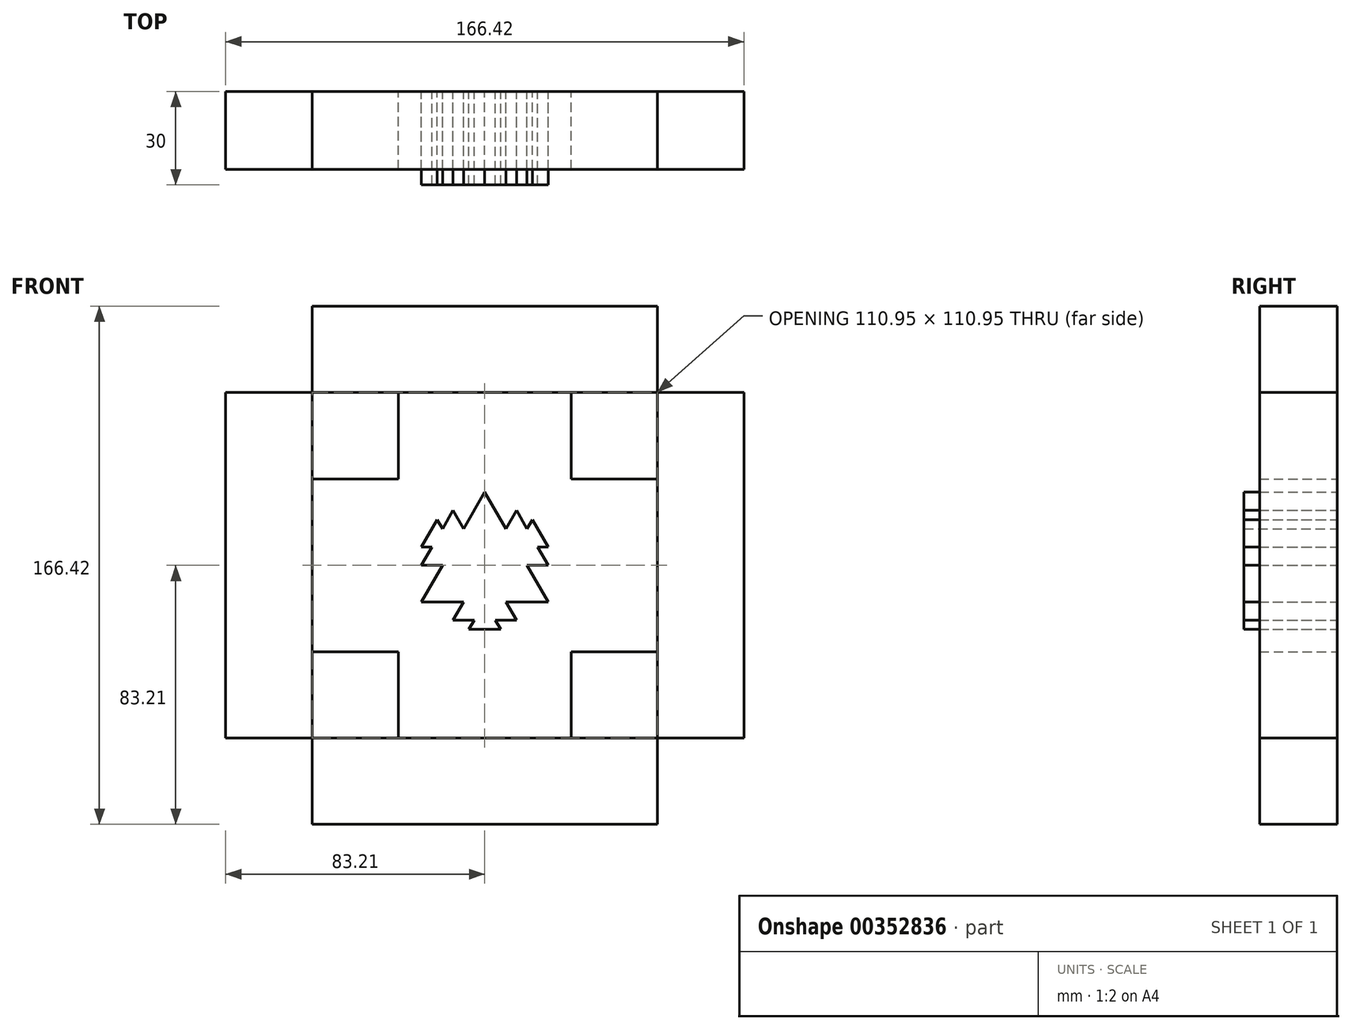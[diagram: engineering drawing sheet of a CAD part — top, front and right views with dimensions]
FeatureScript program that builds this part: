
annotation { "Feature Type Name" : "Feature", "Feature Type Description" : "" }
export const myFeature = defineFeature(function(context is Context, id is Id, definition is map)
    precondition{}
    {
        {
            var Q0;
            Q0=qCreatedBy(makeId("Front.planeOp"),FACE);
            var sketch = newSketch(context, id + "F0", { "sketchPlane" : qUnion([Q0])});
            skLineSegment(sketch, "E0.0", {"start": v(0, 23.49) * mm, "end": v(6.78, 11.74) * mm});
            skLineSegment(sketch, "E0.1", {"start": v(20.34, -11.74) * mm, "end": v(6.78, -11.74) * mm});
            skLineSegment(sketch, "E0.2", {"start": v(-20.34, -11.74) * mm, "end": v(-13.56, 0) * mm});
            skLineSegment(sketch, "E1.0", {"start": v(0, 0) * mm, "end": v(-20.34, 0) * mm});
            skLineSegment(sketch, "E1.1", {"start": v(-20.34, 0) * mm, "end": v(-10.17, 17.62) * mm});
            skLineSegment(sketch, "E1.2", {"start": v(-10.17, 17.62) * mm, "end": v(0, 0) * mm});
            skLineSegment(sketch, "E2.0", {"start": v(0, 0) * mm, "end": v(10.17, 17.62) * mm});
            skLineSegment(sketch, "E2.1", {"start": v(10.17, 17.62) * mm, "end": v(20.34, 0) * mm});
            skLineSegment(sketch, "E2.2", {"start": v(20.34, 0) * mm, "end": v(0, 0) * mm});
            skLineSegment(sketch, "E3.0", {"start": v(0, 0) * mm, "end": v(10.17, -17.62) * mm});
            skLineSegment(sketch, "E3.1", {"start": v(10.17, -17.62) * mm, "end": v(-10.17, -17.62) * mm});
            skLineSegment(sketch, "E3.2", {"start": v(-10.17, -17.62) * mm, "end": v(0, 0) * mm});
            skPoint(sketch, "E2.cCircle.center.orphan", {"position": v(10.17, 5.87) * mm});
            skPoint(sketch, "E3.cCircle.center.orphan", {"position": v(0, -11.74) * mm});
            skPoint(sketch, "E1.cCircle.center.orphan", {"position": v(-10.17, 5.87) * mm});
            skLineSegment(sketch, "E4.trimOffspring", {"start": v(-6.78, 11.74) * mm, "end": v(0, 23.49) * mm});
            skLineSegment(sketch, "E5.trimOffspring", {"start": v(-6.78, -11.74) * mm, "end": v(-20.34, -11.74) * mm});
            skLineSegment(sketch, "E6.trimOffspring", {"start": v(13.56, 0) * mm, "end": v(20.34, -11.74) * mm});
            skLineSegment(sketch, "E7.0", {"start": v(-10.17, 5.87) * mm, "end": v(-20.34, 5.87) * mm});
            skLineSegment(sketch, "E7.1", {"start": v(-20.34, 5.87) * mm, "end": v(-15.26, 14.68) * mm});
            skLineSegment(sketch, "E7.2", {"start": v(-15.26, 14.68) * mm, "end": v(-10.17, 5.87) * mm});
            skLineSegment(sketch, "E8.0", {"start": v(-10.17, 5.87) * mm, "end": v(-5.09, 14.68) * mm});
            skLineSegment(sketch, "E8.1", {"start": v(-5.09, 14.68) * mm, "end": v(0, 5.87) * mm});
            skLineSegment(sketch, "E8.2", {"start": v(0, 5.87) * mm, "end": v(-10.17, 5.87) * mm});
            skLineSegment(sketch, "E9.0", {"start": v(-10.17, 5.87) * mm, "end": v(-5.09, -2.94) * mm});
            skLineSegment(sketch, "E9.1", {"start": v(-5.09, -2.94) * mm, "end": v(-15.26, -2.94) * mm});
            skLineSegment(sketch, "E9.2", {"start": v(-15.26, -2.94) * mm, "end": v(-10.17, 5.87) * mm});
            skLineSegment(sketch, "E10.0", {"start": v(0, -11.74) * mm, "end": v(-10.17, -11.74) * mm});
            skLineSegment(sketch, "E10.1", {"start": v(-10.17, -11.74) * mm, "end": v(-5.09, -2.94) * mm});
            skLineSegment(sketch, "E10.2", {"start": v(-5.09, -2.94) * mm, "end": v(0, -11.74) * mm});
            skLineSegment(sketch, "E11.0", {"start": v(0, -11.74) * mm, "end": v(5.09, -20.55) * mm});
            skLineSegment(sketch, "E11.1", {"start": v(5.09, -20.55) * mm, "end": v(-5.09, -20.55) * mm});
            skLineSegment(sketch, "E11.2", {"start": v(-5.09, -20.55) * mm, "end": v(0, -11.74) * mm});
            skLineSegment(sketch, "E12.0", {"start": v(0, -11.74) * mm, "end": v(5.09, -2.94) * mm});
            skLineSegment(sketch, "E12.1", {"start": v(5.09, -2.94) * mm, "end": v(10.17, -11.74) * mm});
            skLineSegment(sketch, "E12.2", {"start": v(10.17, -11.74) * mm, "end": v(0, -11.74) * mm});
            skLineSegment(sketch, "E13.0", {"start": v(10.17, 5.87) * mm, "end": v(15.26, -2.94) * mm});
            skLineSegment(sketch, "E13.1", {"start": v(15.26, -2.94) * mm, "end": v(5.09, -2.94) * mm});
            skLineSegment(sketch, "E13.2", {"start": v(5.09, -2.94) * mm, "end": v(10.17, 5.87) * mm});
            skLineSegment(sketch, "E14.0", {"start": v(10.17, 5.87) * mm, "end": v(15.26, 14.68) * mm});
            skLineSegment(sketch, "E14.1", {"start": v(15.26, 14.68) * mm, "end": v(20.34, 5.87) * mm});
            skLineSegment(sketch, "E14.2", {"start": v(20.34, 5.87) * mm, "end": v(10.17, 5.87) * mm});
            skLineSegment(sketch, "E15.0", {"start": v(10.17, 5.87) * mm, "end": v(0, 5.87) * mm});
            skLineSegment(sketch, "E15.1", {"start": v(0, 5.87) * mm, "end": v(5.09, 14.68) * mm});
            skLineSegment(sketch, "E15.2", {"start": v(5.09, 14.68) * mm, "end": v(10.17, 5.87) * mm});
            skPoint(sketch, "E7.cCircle.center.orphan", {"position": v(-15.26, 8.8) * mm});
            skPoint(sketch, "E9.cCircle.center.orphan", {"position": v(-10.17, 0) * mm});
            skPoint(sketch, "E8.cCircle.center.orphan", {"position": v(-5.09, 8.8) * mm});
            skPoint(sketch, "E14.cCircle.center.orphan", {"position": v(15.26, 8.8) * mm});
            skPoint(sketch, "E15.cCircle.center.orphan", {"position": v(5.09, 8.8) * mm});
            skPoint(sketch, "E13.cCircle.center.orphan", {"position": v(10.17, 0) * mm});
            skPoint(sketch, "E10.cCircle.center.orphan", {"position": v(-5.09, -8.8) * mm});
            skPoint(sketch, "E12.cCircle.center.orphan", {"position": v(5.09, -8.8) * mm});
            skPoint(sketch, "E11.cCircle.center.orphan", {"position": v(0, -17.62) * mm});
            skSolve(sketch);
        }
        {
            var Q0;
            Q0=makeQuery(id+"F0.imprint","IMPRINT",FACE,{"disambiguationData":[TD([[makeQuery(id+"F0.imprint","IMPRINT",EDGE,{"derivedFrom":sQuery(id+"F0.wireOp",EDGE,"E0.0")}),-1.0]])]});
            var Q1;
            {var subQ5=sQuery(id+"F0.wireOp",EDGE,"E15.1");Q1=makeQuery(id+"F0.imprint","IMPRINT",FACE,{"disambiguationData":[TD([[makeQuery(id+"F0.imprint","IMPRINT",EDGE,{"derivedFrom":subQ5}),-1.0]])]});}
            var Q2;
            {var subQ0=sQuery(id+"F0.wireOp",EDGE,"E15.2");var subQ1=sQuery(id+"F0.wireOp",EDGE,"E2.0");var subQ2=makeQuery(id+"F0.imprint","INTERSECT",VERTEX,{"derivedFrom":[subQ1,subQ0]});Q2=makeQuery(id+"F0.imprint","IMPRINT",FACE,{"disambiguationData":[TD([[makeQuery(id+"F0.imprint","IMPRINT",EDGE,{"disambiguationData":[TD([[subQ2,1.0]])],"derivedFrom":subQ1}),-1.0]])]});}
            var Q3;
            {var subQ0=sQuery(id+"F0.wireOp",EDGE,"E2.1");var subQ1=sQuery(id+"F0.wireOp",EDGE,"E2.0");var subQ2=makeQuery(id+"F0.imprint","INTERSECT",VERTEX,{"derivedFrom":[subQ1,subQ0]});Q3=makeQuery(id+"F0.imprint","IMPRINT",FACE,{"disambiguationData":[TD([[makeQuery(id+"F0.imprint","IMPRINT",EDGE,{"disambiguationData":[TD([[subQ2,1.0]])],"derivedFrom":subQ1}),-1.0]])]});}
            var Q4;
            {var subQ0=sQuery(id+"F0.wireOp",EDGE,"E14.0");var subQ1=sQuery(id+"F0.wireOp",EDGE,"E2.1");var subQ2=makeQuery(id+"F0.imprint","INTERSECT",VERTEX,{"derivedFrom":[subQ1,subQ0]});Q4=makeQuery(id+"F0.imprint","IMPRINT",FACE,{"disambiguationData":[TD([[makeQuery(id+"F0.imprint","IMPRINT",EDGE,{"disambiguationData":[TD([[subQ2,-1.0]])],"derivedFrom":subQ1}),-1.0]])]});}
            var Q5;
            {var subQ5=sQuery(id+"F0.wireOp",EDGE,"E14.1");Q5=makeQuery(id+"F0.imprint","IMPRINT",FACE,{"disambiguationData":[TD([[makeQuery(id+"F0.imprint","IMPRINT",EDGE,{"derivedFrom":subQ5}),-1.0]])]});}
            var Q6;
            {var subQ0=sQuery(id+"F0.wireOp",EDGE,"E2.2");var subQ1=sQuery(id+"F0.wireOp",EDGE,"E2.1");var subQ2=makeQuery(id+"F0.imprint","INTERSECT",VERTEX,{"derivedFrom":[subQ1,subQ0]});Q6=makeQuery(id+"F0.imprint","IMPRINT",FACE,{"disambiguationData":[TD([[makeQuery(id+"F0.imprint","IMPRINT",EDGE,{"disambiguationData":[TD([[subQ2,1.0]])],"derivedFrom":subQ1}),-1.0]])]});}
            var Q7;
            {var subQ0=sQuery(id+"F0.wireOp",EDGE,"E13.0");var subQ1=sQuery(id+"F0.wireOp",EDGE,"E2.2");var subQ2=makeQuery(id+"F0.imprint","INTERSECT",VERTEX,{"derivedFrom":[subQ1,subQ0]});Q7=makeQuery(id+"F0.imprint","IMPRINT",FACE,{"disambiguationData":[TD([[makeQuery(id+"F0.imprint","IMPRINT",EDGE,{"disambiguationData":[TD([[subQ2,-1.0]])],"derivedFrom":subQ1}),-1.0]])]});}
            var Q8;
            {var subQ1=sQuery(id+"F0.wireOp",EDGE,"E2.0");var subQ3=sQuery(id+"F0.wireOp",EDGE,"E15.0");var subQ4=makeQuery(id+"F0.imprint","INTERSECT",VERTEX,{"derivedFrom":[subQ1,subQ3]});Q8=makeQuery(id+"F0.imprint","IMPRINT",FACE,{"disambiguationData":[TD([[makeQuery(id+"F0.imprint","IMPRINT",EDGE,{"disambiguationData":[TD([[subQ4,1.0]])],"derivedFrom":subQ1}),-1.0]])]});}
            var Q9;
            {var subQ5=sQuery(id+"F0.wireOp",EDGE,"E8.1");Q9=makeQuery(id+"F0.imprint","IMPRINT",FACE,{"disambiguationData":[TD([[makeQuery(id+"F0.imprint","IMPRINT",EDGE,{"derivedFrom":subQ5}),-1.0]])]});}
            var Q10;
            {var subQ0=sQuery(id+"F0.wireOp",EDGE,"E8.0");var subQ1=sQuery(id+"F0.wireOp",EDGE,"E1.2");var subQ2=makeQuery(id+"F0.imprint","INTERSECT",VERTEX,{"derivedFrom":[subQ1,subQ0]});Q10=makeQuery(id+"F0.imprint","IMPRINT",FACE,{"disambiguationData":[TD([[makeQuery(id+"F0.imprint","IMPRINT",EDGE,{"disambiguationData":[TD([[subQ2,-1.0]])],"derivedFrom":subQ1}),-1.0]])]});}
            var Q11;
            {var subQ0=sQuery(id+"F0.wireOp",EDGE,"E1.2");var subQ1=sQuery(id+"F0.wireOp",EDGE,"E1.1");var subQ2=makeQuery(id+"F0.imprint","INTERSECT",VERTEX,{"derivedFrom":[subQ1,subQ0]});Q11=makeQuery(id+"F0.imprint","IMPRINT",FACE,{"disambiguationData":[TD([[makeQuery(id+"F0.imprint","IMPRINT",EDGE,{"disambiguationData":[TD([[subQ2,1.0]])],"derivedFrom":subQ1}),-1.0]])]});}
            var Q12;
            {var subQ5=sQuery(id+"F0.wireOp",EDGE,"E7.1");Q12=makeQuery(id+"F0.imprint","IMPRINT",FACE,{"disambiguationData":[TD([[makeQuery(id+"F0.imprint","IMPRINT",EDGE,{"derivedFrom":subQ5}),-1.0]])]});}
            var Q13;
            {var subQ0=sQuery(id+"F0.wireOp",EDGE,"E7.0");var subQ1=sQuery(id+"F0.wireOp",EDGE,"E1.1");var subQ2=makeQuery(id+"F0.imprint","INTERSECT",VERTEX,{"derivedFrom":[subQ1,subQ0]});Q13=makeQuery(id+"F0.imprint","IMPRINT",FACE,{"disambiguationData":[TD([[makeQuery(id+"F0.imprint","IMPRINT",EDGE,{"disambiguationData":[TD([[subQ2,-1.0]])],"derivedFrom":subQ1}),-1.0]])]});}
            var Q14;
            {var subQ0=sQuery(id+"F0.wireOp",EDGE,"E1.1");var subQ1=sQuery(id+"F0.wireOp",EDGE,"E1.0");var subQ2=makeQuery(id+"F0.imprint","INTERSECT",VERTEX,{"derivedFrom":[subQ1,subQ0]});Q14=makeQuery(id+"F0.imprint","IMPRINT",FACE,{"disambiguationData":[TD([[makeQuery(id+"F0.imprint","IMPRINT",EDGE,{"disambiguationData":[TD([[subQ2,1.0]])],"derivedFrom":subQ1}),-1.0]])]});}
            var Q15;
            {var subQ0=sQuery(id+"F0.wireOp",EDGE,"E9.2");var subQ1=sQuery(id+"F0.wireOp",EDGE,"E1.0");var subQ2=makeQuery(id+"F0.imprint","INTERSECT",VERTEX,{"derivedFrom":[subQ1,subQ0]});Q15=makeQuery(id+"F0.imprint","IMPRINT",FACE,{"disambiguationData":[TD([[makeQuery(id+"F0.imprint","IMPRINT",EDGE,{"disambiguationData":[TD([[subQ2,1.0]])],"derivedFrom":subQ1}),-1.0]])]});}
            var Q16;
            {var subQ1=sQuery(id+"F0.wireOp",EDGE,"E1.0");var subQ3=sQuery(id+"F0.wireOp",EDGE,"E9.0");var subQ4=makeQuery(id+"F0.imprint","INTERSECT",VERTEX,{"derivedFrom":[subQ1,subQ3]});Q16=makeQuery(id+"F0.imprint","IMPRINT",FACE,{"disambiguationData":[TD([[makeQuery(id+"F0.imprint","IMPRINT",EDGE,{"disambiguationData":[TD([[subQ4,1.0]])],"derivedFrom":subQ1}),-1.0]])]});}
            var Q17;
            {var subQ1=sQuery(id+"F0.wireOp",EDGE,"E1.2");var subQ3=sQuery(id+"F0.wireOp",EDGE,"E8.2");var subQ4=makeQuery(id+"F0.imprint","INTERSECT",VERTEX,{"derivedFrom":[subQ1,subQ3]});Q17=makeQuery(id+"F0.imprint","IMPRINT",FACE,{"disambiguationData":[TD([[makeQuery(id+"F0.imprint","IMPRINT",EDGE,{"disambiguationData":[TD([[subQ4,1.0]])],"derivedFrom":subQ3}),1.0]])]});}
            var Q18;
            {var subQ5=sQuery(id+"F0.wireOp",EDGE,"E13.1");Q18=makeQuery(id+"F0.imprint","IMPRINT",FACE,{"disambiguationData":[TD([[makeQuery(id+"F0.imprint","IMPRINT",EDGE,{"derivedFrom":subQ5}),-1.0]])]});}
            var Q19;
            Q19=makeQuery(id+"F0.imprint","IMPRINT",FACE,{"disambiguationData":[TD([[makeQuery(id+"F0.imprint","IMPRINT",EDGE,{"derivedFrom":sQuery(id+"F0.wireOp",EDGE,"E0.1")}),-1.0]])]});
            var Q20;
            {var subQ5=sQuery(id+"F0.wireOp",EDGE,"E12.1");Q20=makeQuery(id+"F0.imprint","IMPRINT",FACE,{"disambiguationData":[TD([[makeQuery(id+"F0.imprint","IMPRINT",EDGE,{"derivedFrom":subQ5}),-1.0]])]});}
            var Q21;
            {var subQ0=sQuery(id+"F0.wireOp",EDGE,"E12.2");var subQ1=sQuery(id+"F0.wireOp",EDGE,"E3.0");var subQ2=makeQuery(id+"F0.imprint","INTERSECT",VERTEX,{"derivedFrom":[subQ1,subQ0]});Q21=makeQuery(id+"F0.imprint","IMPRINT",FACE,{"disambiguationData":[TD([[makeQuery(id+"F0.imprint","IMPRINT",EDGE,{"disambiguationData":[TD([[subQ2,1.0]])],"derivedFrom":subQ1}),-1.0]])]});}
            var Q22;
            {var subQ1=sQuery(id+"F0.wireOp",EDGE,"E3.0");var subQ3=sQuery(id+"F0.wireOp",EDGE,"E12.0");var subQ4=makeQuery(id+"F0.imprint","INTERSECT",VERTEX,{"derivedFrom":[subQ1,subQ3]});Q22=makeQuery(id+"F0.imprint","IMPRINT",FACE,{"disambiguationData":[TD([[makeQuery(id+"F0.imprint","IMPRINT",EDGE,{"disambiguationData":[TD([[subQ4,1.0]])],"derivedFrom":subQ1}),-1.0]])]});}
            var Q23;
            {var subQ0=sQuery(id+"F0.wireOp",EDGE,"E3.0");var subQ5=sQuery(id+"F0.wireOp",EDGE,"E12.0");var subQ6=makeQuery(id+"F0.imprint","INTERSECT",VERTEX,{"derivedFrom":[subQ0,subQ5]});Q23=makeQuery(id+"F0.imprint","IMPRINT",FACE,{"disambiguationData":[TD([[makeQuery(id+"F0.imprint","IMPRINT",EDGE,{"disambiguationData":[TD([[subQ6,-1.0]])],"derivedFrom":subQ5}),1.0]])]});}
            var Q24;
            {var subQ1=sQuery(id+"F0.wireOp",EDGE,"E1.0");var subQ3=sQuery(id+"F0.wireOp",EDGE,"E9.0");var subQ4=makeQuery(id+"F0.imprint","INTERSECT",VERTEX,{"derivedFrom":[subQ1,subQ3]});Q24=makeQuery(id+"F0.imprint","IMPRINT",FACE,{"disambiguationData":[TD([[makeQuery(id+"F0.imprint","IMPRINT",EDGE,{"disambiguationData":[TD([[subQ4,-1.0]])],"derivedFrom":subQ3}),1.0]])]});}
            var Q25;
            {var subQ5=sQuery(id+"F0.wireOp",EDGE,"E10.1");Q25=makeQuery(id+"F0.imprint","IMPRINT",FACE,{"disambiguationData":[TD([[makeQuery(id+"F0.imprint","IMPRINT",EDGE,{"derivedFrom":subQ5}),-1.0]])]});}
            var Q26;
            {var subQ5=sQuery(id+"F0.wireOp",EDGE,"E9.1");Q26=makeQuery(id+"F0.imprint","IMPRINT",FACE,{"disambiguationData":[TD([[makeQuery(id+"F0.imprint","IMPRINT",EDGE,{"derivedFrom":subQ5}),-1.0]])]});}
            var Q27;
            Q27=makeQuery(id+"F0.imprint","IMPRINT",FACE,{"disambiguationData":[TD([[makeQuery(id+"F0.imprint","IMPRINT",EDGE,{"derivedFrom":sQuery(id+"F0.wireOp",EDGE,"E0.2")}),-1.0]])]});
            var Q28;
            {var subQ0=sQuery(id+"F0.wireOp",EDGE,"E10.0");var subQ1=sQuery(id+"F0.wireOp",EDGE,"E3.2");var subQ2=makeQuery(id+"F0.imprint","INTERSECT",VERTEX,{"derivedFrom":[subQ1,subQ0]});Q28=makeQuery(id+"F0.imprint","IMPRINT",FACE,{"disambiguationData":[TD([[makeQuery(id+"F0.imprint","IMPRINT",EDGE,{"disambiguationData":[TD([[subQ2,-1.0]])],"derivedFrom":subQ1}),-1.0]])]});}
            var Q29;
            {var subQ0=sQuery(id+"F0.wireOp",EDGE,"E3.2");var subQ1=sQuery(id+"F0.wireOp",EDGE,"E3.1");var subQ2=makeQuery(id+"F0.imprint","INTERSECT",VERTEX,{"derivedFrom":[subQ1,subQ0]});Q29=makeQuery(id+"F0.imprint","IMPRINT",FACE,{"disambiguationData":[TD([[makeQuery(id+"F0.imprint","IMPRINT",EDGE,{"disambiguationData":[TD([[subQ2,1.0]])],"derivedFrom":subQ1}),-1.0]])]});}
            var Q30;
            {var subQ0=sQuery(id+"F0.wireOp",EDGE,"E11.0");var subQ1=sQuery(id+"F0.wireOp",EDGE,"E3.1");var subQ2=makeQuery(id+"F0.imprint","INTERSECT",VERTEX,{"derivedFrom":[subQ1,subQ0]});Q30=makeQuery(id+"F0.imprint","IMPRINT",FACE,{"disambiguationData":[TD([[makeQuery(id+"F0.imprint","IMPRINT",EDGE,{"disambiguationData":[TD([[subQ2,-1.0]])],"derivedFrom":subQ1}),-1.0]])]});}
            var Q31;
            {var subQ0=sQuery(id+"F0.wireOp",EDGE,"E3.1");var subQ1=sQuery(id+"F0.wireOp",EDGE,"E3.0");var subQ2=makeQuery(id+"F0.imprint","INTERSECT",VERTEX,{"derivedFrom":[subQ1,subQ0]});Q31=makeQuery(id+"F0.imprint","IMPRINT",FACE,{"disambiguationData":[TD([[makeQuery(id+"F0.imprint","IMPRINT",EDGE,{"disambiguationData":[TD([[subQ2,1.0]])],"derivedFrom":subQ1}),-1.0]])]});}
            var Q32;
            {var subQ5=sQuery(id+"F0.wireOp",EDGE,"E11.1");Q32=makeQuery(id+"F0.imprint","IMPRINT",FACE,{"disambiguationData":[TD([[makeQuery(id+"F0.imprint","IMPRINT",EDGE,{"derivedFrom":subQ5}),-1.0]])]});}
            extrude(context, id + "F1", {"entities" : qUnion([Q0, Q1, Q2, Q3, Q4, Q5, Q6, Q7, Q8, Q9, Q10, Q11, Q12, Q13, Q14, Q15, Q16, Q17, Q18, Q19, Q20, Q21, Q22, Q23, Q24, Q25, Q26, Q27, Q28, Q29, Q30, Q31, Q32]), "depth" : 30 * mm});
        }
        {
            var Q0;
            Q0=qCreatedBy(makeId("Front.planeOp"),FACE);
            var sketch = newSketch(context, id + "F2", { "sketchPlane" : qUnion([Q0])});
            skLineSegment(sketch, "E16.0", {"start": v(0, 55.48) * mm, "end": v(55.48, 0) * mm});
            skLineSegment(sketch, "E16.1", {"start": v(55.48, 0) * mm, "end": v(0, -55.48) * mm});
            skLineSegment(sketch, "E16.2", {"start": v(0, -55.48) * mm, "end": v(-55.48, 0) * mm});
            skLineSegment(sketch, "E16.3", {"start": v(-55.48, 0) * mm, "end": v(0, 55.48) * mm});
            skLineSegment(sketch, "E17.0", {"start": v(0, 0) * mm, "end": v(0, 55.48) * mm});
            skLineSegment(sketch, "E17.1", {"start": v(0, 55.48) * mm, "end": v(55.48, 55.48) * mm});
            skLineSegment(sketch, "E17.2", {"start": v(55.48, 55.48) * mm, "end": v(55.48, 0) * mm});
            skLineSegment(sketch, "E17.3", {"start": v(55.48, 0) * mm, "end": v(0, 0) * mm});
            skLineSegment(sketch, "E18.0", {"start": v(0, 0) * mm, "end": v(-55.48, 0) * mm});
            skLineSegment(sketch, "E18.1", {"start": v(-55.48, 0) * mm, "end": v(-55.48, 55.48) * mm});
            skLineSegment(sketch, "E18.2", {"start": v(-55.48, 55.48) * mm, "end": v(0, 55.48) * mm});
            skLineSegment(sketch, "E18.3", {"start": v(0, 55.48) * mm, "end": v(0, 0) * mm});
            skLineSegment(sketch, "E19.0", {"start": v(0, 0) * mm, "end": v(0, -55.48) * mm});
            skLineSegment(sketch, "E19.1", {"start": v(0, -55.48) * mm, "end": v(-55.48, -55.48) * mm});
            skLineSegment(sketch, "E19.2", {"start": v(-55.48, -55.48) * mm, "end": v(-55.48, 0) * mm});
            skLineSegment(sketch, "E19.3", {"start": v(-55.48, 0) * mm, "end": v(0, 0) * mm});
            skLineSegment(sketch, "E20.0", {"start": v(0, 0) * mm, "end": v(55.48, 0) * mm});
            skLineSegment(sketch, "E20.1", {"start": v(55.48, 0) * mm, "end": v(55.48, -55.48) * mm});
            skLineSegment(sketch, "E20.2", {"start": v(55.48, -55.48) * mm, "end": v(0, -55.48) * mm});
            skLineSegment(sketch, "E20.3", {"start": v(0, -55.48) * mm, "end": v(0, 0) * mm});
            skPoint(sketch, "E20.cCircle.center.orphan", {"position": v(27.74, -27.74) * mm});
            skPoint(sketch, "E17.cCircle.center.orphan", {"position": v(27.74, 27.74) * mm});
            skPoint(sketch, "E18.cCircle.center.orphan", {"position": v(-27.74, 27.74) * mm});
            skPoint(sketch, "E19.cCircle.center.orphan", {"position": v(-27.74, -27.74) * mm});
            skLineSegment(sketch, "E21.0", {"start": v(27.74, 27.74) * mm, "end": v(0, 55.48) * mm});
            skLineSegment(sketch, "E21.1", {"start": v(0, 55.48) * mm, "end": v(27.74, 83.21) * mm});
            skLineSegment(sketch, "E21.2", {"start": v(27.74, 83.21) * mm, "end": v(55.48, 55.48) * mm});
            skLineSegment(sketch, "E21.3", {"start": v(55.48, 55.48) * mm, "end": v(27.74, 27.74) * mm});
            skLineSegment(sketch, "E22.0", {"start": v(27.74, 27.74) * mm, "end": v(55.48, 55.48) * mm});
            skLineSegment(sketch, "E22.1", {"start": v(55.48, 55.48) * mm, "end": v(83.21, 27.74) * mm});
            skLineSegment(sketch, "E22.2", {"start": v(83.21, 27.74) * mm, "end": v(55.48, 0) * mm});
            skLineSegment(sketch, "E22.3", {"start": v(55.48, 0) * mm, "end": v(27.74, 27.74) * mm});
            skLineSegment(sketch, "E23.0", {"start": v(27.74, 27.74) * mm, "end": v(55.48, 0) * mm});
            skLineSegment(sketch, "E23.1", {"start": v(55.48, 0) * mm, "end": v(27.74, -27.74) * mm});
            skLineSegment(sketch, "E23.2", {"start": v(27.74, -27.74) * mm, "end": v(0, 0) * mm});
            skLineSegment(sketch, "E23.3", {"start": v(0, 0) * mm, "end": v(27.74, 27.74) * mm});
            skLineSegment(sketch, "E24.0", {"start": v(27.74, 27.74) * mm, "end": v(0, 0) * mm});
            skLineSegment(sketch, "E24.1", {"start": v(0, 0) * mm, "end": v(-27.74, 27.74) * mm});
            skLineSegment(sketch, "E24.2", {"start": v(-27.74, 27.74) * mm, "end": v(0, 55.48) * mm});
            skLineSegment(sketch, "E24.3", {"start": v(0, 55.48) * mm, "end": v(27.74, 27.74) * mm});
            skLineSegment(sketch, "E25.0", {"start": v(27.74, -27.74) * mm, "end": v(55.48, 0) * mm});
            skLineSegment(sketch, "E25.1", {"start": v(55.48, 0) * mm, "end": v(83.21, -27.74) * mm});
            skLineSegment(sketch, "E25.2", {"start": v(83.21, -27.74) * mm, "end": v(55.48, -55.48) * mm});
            skLineSegment(sketch, "E25.3", {"start": v(55.48, -55.48) * mm, "end": v(27.74, -27.74) * mm});
            skLineSegment(sketch, "E26.0", {"start": v(27.74, -27.74) * mm, "end": v(55.48, -55.48) * mm});
            skLineSegment(sketch, "E26.1", {"start": v(55.48, -55.48) * mm, "end": v(27.74, -83.21) * mm});
            skLineSegment(sketch, "E26.2", {"start": v(27.74, -83.21) * mm, "end": v(0, -55.48) * mm});
            skLineSegment(sketch, "E26.3", {"start": v(0, -55.48) * mm, "end": v(27.74, -27.74) * mm});
            skLineSegment(sketch, "E27.0", {"start": v(27.74, -27.74) * mm, "end": v(0, -55.48) * mm});
            skLineSegment(sketch, "E27.1", {"start": v(0, -55.48) * mm, "end": v(-27.74, -27.74) * mm});
            skLineSegment(sketch, "E27.2", {"start": v(-27.74, -27.74) * mm, "end": v(0, 0) * mm});
            skLineSegment(sketch, "E27.3", {"start": v(0, 0) * mm, "end": v(27.74, -27.74) * mm});
            skLineSegment(sketch, "E28.0", {"start": v(-27.74, -27.74) * mm, "end": v(0, -55.48) * mm});
            skLineSegment(sketch, "E28.1", {"start": v(0, -55.48) * mm, "end": v(-27.74, -83.21) * mm});
            skLineSegment(sketch, "E28.2", {"start": v(-27.74, -83.21) * mm, "end": v(-55.48, -55.48) * mm});
            skLineSegment(sketch, "E28.3", {"start": v(-55.48, -55.48) * mm, "end": v(-27.74, -27.74) * mm});
            skLineSegment(sketch, "E29.0", {"start": v(-27.74, -27.74) * mm, "end": v(-55.48, -55.48) * mm});
            skLineSegment(sketch, "E29.1", {"start": v(-55.48, -55.48) * mm, "end": v(-83.21, -27.74) * mm});
            skLineSegment(sketch, "E29.2", {"start": v(-83.21, -27.74) * mm, "end": v(-55.48, 0) * mm});
            skLineSegment(sketch, "E29.3", {"start": v(-55.48, 0) * mm, "end": v(-27.74, -27.74) * mm});
            skLineSegment(sketch, "E30.0", {"start": v(-27.74, -27.74) * mm, "end": v(-55.48, 0) * mm});
            skLineSegment(sketch, "E30.1", {"start": v(-55.48, 0) * mm, "end": v(-27.74, 27.74) * mm});
            skLineSegment(sketch, "E30.2", {"start": v(-27.74, 27.74) * mm, "end": v(0, 0) * mm});
            skLineSegment(sketch, "E30.3", {"start": v(0, 0) * mm, "end": v(-27.74, -27.74) * mm});
            skLineSegment(sketch, "E31.0", {"start": v(-27.74, 27.74) * mm, "end": v(-55.48, 0) * mm});
            skLineSegment(sketch, "E31.1", {"start": v(-55.48, 0) * mm, "end": v(-83.21, 27.74) * mm});
            skLineSegment(sketch, "E31.2", {"start": v(-83.21, 27.74) * mm, "end": v(-55.48, 55.48) * mm});
            skLineSegment(sketch, "E31.3", {"start": v(-55.48, 55.48) * mm, "end": v(-27.74, 27.74) * mm});
            skLineSegment(sketch, "E32.0", {"start": v(-27.74, 27.74) * mm, "end": v(-55.48, 55.48) * mm});
            skLineSegment(sketch, "E32.1", {"start": v(-55.48, 55.48) * mm, "end": v(-27.74, 83.21) * mm});
            skLineSegment(sketch, "E32.2", {"start": v(-27.74, 83.21) * mm, "end": v(0, 55.48) * mm});
            skLineSegment(sketch, "E32.3", {"start": v(0, 55.48) * mm, "end": v(-27.74, 27.74) * mm});
            skPoint(sketch, "E32.cCircle.center.orphan", {"position": v(-27.74, 55.48) * mm});
            skPoint(sketch, "E21.cCircle.center.orphan", {"position": v(27.74, 55.48) * mm});
            skPoint(sketch, "E24.cCircle.center.orphan", {"position": v(0, 27.74) * mm});
            skPoint(sketch, "E22.cCircle.center.orphan", {"position": v(55.48, 27.74) * mm});
            skPoint(sketch, "E27.cCircle.center.orphan", {"position": v(0, -27.74) * mm});
            skPoint(sketch, "E23.cCircle.center.orphan", {"position": v(27.74, 0) * mm});
            skPoint(sketch, "E25.cCircle.center.orphan", {"position": v(55.48, -27.74) * mm});
            skPoint(sketch, "E26.cCircle.center.orphan", {"position": v(27.74, -55.48) * mm});
            skPoint(sketch, "E28.cCircle.center.orphan", {"position": v(-27.74, -55.48) * mm});
            skPoint(sketch, "E33.cCircle.center.orphan", {"position": v(-27.74, 0) * mm});
            skPoint(sketch, "E29.cCircle.center.orphan", {"position": v(-55.48, -27.74) * mm});
            skPoint(sketch, "E31.cCircle.center.orphan", {"position": v(-55.48, 27.74) * mm});
            skCircle(sketch, "E34.cCircle", {"center": v(-41.6, 69.34) * mm, "radius": 19.61 * mm, "construction": true});
            skLineSegment(sketch, "E34.0", {"start": v(-27.74, 55.48) * mm, "end": v(-55.48, 55.48) * mm});
            skLineSegment(sketch, "E34.1", {"start": v(-55.48, 55.48) * mm, "end": v(-55.48, 83.21) * mm});
            skLineSegment(sketch, "E34.2", {"start": v(-55.48, 83.21) * mm, "end": v(-27.74, 83.21) * mm});
            skLineSegment(sketch, "E34.3", {"start": v(-27.74, 83.21) * mm, "end": v(-27.74, 55.48) * mm});
            skCircle(sketch, "E35.cCircle", {"center": v(-13.87, 69.34) * mm, "radius": 19.61 * mm, "construction": true});
            skLineSegment(sketch, "E35.0", {"start": v(-27.74, 55.48) * mm, "end": v(-27.74, 83.21) * mm});
            skLineSegment(sketch, "E35.1", {"start": v(-27.74, 83.21) * mm, "end": v(0, 83.21) * mm});
            skLineSegment(sketch, "E35.2", {"start": v(0, 83.21) * mm, "end": v(0, 55.48) * mm});
            skLineSegment(sketch, "E35.3", {"start": v(0, 55.48) * mm, "end": v(-27.74, 55.48) * mm});
            skCircle(sketch, "E36.cCircle", {"center": v(13.87, 69.34) * mm, "radius": 19.61 * mm, "construction": true});
            skLineSegment(sketch, "E36.0", {"start": v(27.74, 55.48) * mm, "end": v(0, 55.48) * mm});
            skLineSegment(sketch, "E36.1", {"start": v(0, 55.48) * mm, "end": v(0, 83.21) * mm});
            skLineSegment(sketch, "E36.2", {"start": v(0, 83.21) * mm, "end": v(27.74, 83.21) * mm});
            skLineSegment(sketch, "E36.3", {"start": v(27.74, 83.21) * mm, "end": v(27.74, 55.48) * mm});
            skCircle(sketch, "E37.cCircle", {"center": v(41.6, 69.34) * mm, "radius": 19.61 * mm, "construction": true});
            skLineSegment(sketch, "E37.0", {"start": v(27.74, 55.48) * mm, "end": v(27.74, 83.21) * mm});
            skLineSegment(sketch, "E37.1", {"start": v(27.74, 83.21) * mm, "end": v(55.48, 83.21) * mm});
            skLineSegment(sketch, "E37.2", {"start": v(55.48, 83.21) * mm, "end": v(55.48, 55.48) * mm});
            skLineSegment(sketch, "E37.3", {"start": v(55.48, 55.48) * mm, "end": v(27.74, 55.48) * mm});
            skCircle(sketch, "E38.cCircle", {"center": v(-69.34, 41.6) * mm, "radius": 19.61 * mm, "construction": true});
            skLineSegment(sketch, "E38.0", {"start": v(-55.48, 27.74) * mm, "end": v(-83.21, 27.74) * mm});
            skLineSegment(sketch, "E38.1", {"start": v(-83.21, 27.74) * mm, "end": v(-83.21, 55.48) * mm});
            skLineSegment(sketch, "E38.2", {"start": v(-83.21, 55.48) * mm, "end": v(-55.48, 55.48) * mm});
            skLineSegment(sketch, "E38.3", {"start": v(-55.48, 55.48) * mm, "end": v(-55.48, 27.74) * mm});
            skCircle(sketch, "E39.cCircle", {"center": v(-41.6, 41.6) * mm, "radius": 19.61 * mm, "construction": true});
            skLineSegment(sketch, "E39.0", {"start": v(-55.48, 27.74) * mm, "end": v(-55.48, 55.48) * mm});
            skLineSegment(sketch, "E39.1", {"start": v(-55.48, 55.48) * mm, "end": v(-27.74, 55.48) * mm});
            skLineSegment(sketch, "E39.2", {"start": v(-27.74, 55.48) * mm, "end": v(-27.74, 27.74) * mm});
            skLineSegment(sketch, "E39.3", {"start": v(-27.74, 27.74) * mm, "end": v(-55.48, 27.74) * mm});
            skCircle(sketch, "E40.cCircle", {"center": v(-13.87, 41.6) * mm, "radius": 19.61 * mm, "construction": true});
            skLineSegment(sketch, "E40.0", {"start": v(-27.74, 27.74) * mm, "end": v(-27.74, 55.48) * mm});
            skLineSegment(sketch, "E40.1", {"start": v(-27.74, 55.48) * mm, "end": v(0, 55.48) * mm});
            skLineSegment(sketch, "E40.2", {"start": v(0, 55.48) * mm, "end": v(0, 27.74) * mm});
            skLineSegment(sketch, "E40.3", {"start": v(0, 27.74) * mm, "end": v(-27.74, 27.74) * mm});
            skCircle(sketch, "E41.cCircle", {"center": v(13.87, 41.6) * mm, "radius": 19.61 * mm, "construction": true});
            skLineSegment(sketch, "E41.0", {"start": v(0, 27.74) * mm, "end": v(0, 55.48) * mm});
            skLineSegment(sketch, "E41.1", {"start": v(0, 55.48) * mm, "end": v(27.74, 55.48) * mm});
            skLineSegment(sketch, "E41.2", {"start": v(27.74, 55.48) * mm, "end": v(27.74, 27.74) * mm});
            skLineSegment(sketch, "E41.3", {"start": v(27.74, 27.74) * mm, "end": v(0, 27.74) * mm});
            skCircle(sketch, "E42.cCircle", {"center": v(41.6, 41.6) * mm, "radius": 19.61 * mm, "construction": true});
            skLineSegment(sketch, "E42.0", {"start": v(27.74, 27.74) * mm, "end": v(27.74, 55.48) * mm});
            skLineSegment(sketch, "E42.1", {"start": v(27.74, 55.48) * mm, "end": v(55.48, 55.48) * mm});
            skLineSegment(sketch, "E42.2", {"start": v(55.48, 55.48) * mm, "end": v(55.48, 27.74) * mm});
            skLineSegment(sketch, "E42.3", {"start": v(55.48, 27.74) * mm, "end": v(27.74, 27.74) * mm});
            skCircle(sketch, "E43.cCircle", {"center": v(69.34, 41.6) * mm, "radius": 19.61 * mm, "construction": true});
            skLineSegment(sketch, "E43.0", {"start": v(55.48, 27.74) * mm, "end": v(55.48, 55.48) * mm});
            skLineSegment(sketch, "E43.1", {"start": v(55.48, 55.48) * mm, "end": v(83.21, 55.48) * mm});
            skLineSegment(sketch, "E43.2", {"start": v(83.21, 55.48) * mm, "end": v(83.21, 27.74) * mm});
            skLineSegment(sketch, "E43.3", {"start": v(83.21, 27.74) * mm, "end": v(55.48, 27.74) * mm});
            skCircle(sketch, "E44.cCircle", {"center": v(69.34, 13.87) * mm, "radius": 19.61 * mm, "construction": true});
            skLineSegment(sketch, "E44.0", {"start": v(55.48, 0) * mm, "end": v(55.48, 27.74) * mm});
            skLineSegment(sketch, "E44.1", {"start": v(55.48, 27.74) * mm, "end": v(83.21, 27.74) * mm});
            skLineSegment(sketch, "E44.2", {"start": v(83.21, 27.74) * mm, "end": v(83.21, 0) * mm});
            skLineSegment(sketch, "E44.3", {"start": v(83.21, 0) * mm, "end": v(55.48, 0) * mm});
            skCircle(sketch, "E45.cCircle", {"center": v(41.6, 13.87) * mm, "radius": 19.61 * mm, "construction": true});
            skLineSegment(sketch, "E45.0", {"start": v(27.74, 0) * mm, "end": v(27.74, 27.74) * mm});
            skLineSegment(sketch, "E45.1", {"start": v(27.74, 27.74) * mm, "end": v(55.48, 27.74) * mm});
            skLineSegment(sketch, "E45.2", {"start": v(55.48, 27.74) * mm, "end": v(55.48, 0) * mm});
            skLineSegment(sketch, "E45.3", {"start": v(55.48, 0) * mm, "end": v(27.74, 0) * mm});
            skCircle(sketch, "E46.cCircle", {"center": v(13.87, 13.87) * mm, "radius": 19.61 * mm, "construction": true});
            skLineSegment(sketch, "E46.0", {"start": v(0, 0) * mm, "end": v(0, 27.74) * mm});
            skLineSegment(sketch, "E46.1", {"start": v(0, 27.74) * mm, "end": v(27.74, 27.74) * mm});
            skLineSegment(sketch, "E46.2", {"start": v(27.74, 27.74) * mm, "end": v(27.74, 0) * mm});
            skLineSegment(sketch, "E46.3", {"start": v(27.74, 0) * mm, "end": v(0, 0) * mm});
            skCircle(sketch, "E47.cCircle", {"center": v(-13.87, 13.87) * mm, "radius": 19.61 * mm, "construction": true});
            skLineSegment(sketch, "E47.0", {"start": v(-27.74, 0) * mm, "end": v(-27.74, 27.74) * mm});
            skLineSegment(sketch, "E47.1", {"start": v(-27.74, 27.74) * mm, "end": v(0, 27.74) * mm});
            skLineSegment(sketch, "E47.2", {"start": v(0, 27.74) * mm, "end": v(0, 0) * mm});
            skLineSegment(sketch, "E47.3", {"start": v(0, 0) * mm, "end": v(-27.74, 0) * mm});
            skCircle(sketch, "E48.cCircle", {"center": v(-41.6, 13.87) * mm, "radius": 19.61 * mm, "construction": true});
            skLineSegment(sketch, "E48.0", {"start": v(-55.48, 0) * mm, "end": v(-55.48, 27.74) * mm});
            skLineSegment(sketch, "E48.1", {"start": v(-55.48, 27.74) * mm, "end": v(-27.74, 27.74) * mm});
            skLineSegment(sketch, "E48.2", {"start": v(-27.74, 27.74) * mm, "end": v(-27.74, 0) * mm});
            skLineSegment(sketch, "E48.3", {"start": v(-27.74, 0) * mm, "end": v(-55.48, 0) * mm});
            skCircle(sketch, "E49.cCircle", {"center": v(-69.34, 13.87) * mm, "radius": 19.61 * mm, "construction": true});
            skLineSegment(sketch, "E49.0", {"start": v(-55.48, 27.74) * mm, "end": v(-55.48, 0) * mm});
            skLineSegment(sketch, "E49.1", {"start": v(-55.48, 0) * mm, "end": v(-83.21, 0) * mm});
            skLineSegment(sketch, "E49.2", {"start": v(-83.21, 0) * mm, "end": v(-83.21, 27.74) * mm});
            skLineSegment(sketch, "E49.3", {"start": v(-83.21, 27.74) * mm, "end": v(-55.48, 27.74) * mm});
            skCircle(sketch, "E50.cCircle", {"center": v(-69.34, -13.87) * mm, "radius": 19.61 * mm, "construction": true});
            skLineSegment(sketch, "E50.0", {"start": v(-55.48, -27.74) * mm, "end": v(-83.21, -27.74) * mm});
            skLineSegment(sketch, "E50.1", {"start": v(-83.21, -27.74) * mm, "end": v(-83.21, 0) * mm});
            skLineSegment(sketch, "E50.2", {"start": v(-83.21, 0) * mm, "end": v(-55.48, 0) * mm});
            skLineSegment(sketch, "E50.3", {"start": v(-55.48, 0) * mm, "end": v(-55.48, -27.74) * mm});
            skCircle(sketch, "E51.cCircle", {"center": v(-41.6, -13.87) * mm, "radius": 19.61 * mm, "construction": true});
            skLineSegment(sketch, "E51.0", {"start": v(-55.48, -27.74) * mm, "end": v(-55.48, 0) * mm});
            skLineSegment(sketch, "E51.1", {"start": v(-55.48, 0) * mm, "end": v(-27.74, 0) * mm});
            skLineSegment(sketch, "E51.2", {"start": v(-27.74, 0) * mm, "end": v(-27.74, -27.74) * mm});
            skLineSegment(sketch, "E51.3", {"start": v(-27.74, -27.74) * mm, "end": v(-55.48, -27.74) * mm});
            skCircle(sketch, "E52.cCircle", {"center": v(-13.87, -13.87) * mm, "radius": 19.61 * mm, "construction": true});
            skLineSegment(sketch, "E52.0", {"start": v(-27.74, -27.74) * mm, "end": v(-27.74, 0) * mm});
            skLineSegment(sketch, "E52.1", {"start": v(-27.74, 0) * mm, "end": v(0, 0) * mm});
            skLineSegment(sketch, "E52.2", {"start": v(0, 0) * mm, "end": v(0, -27.74) * mm});
            skLineSegment(sketch, "E52.3", {"start": v(0, -27.74) * mm, "end": v(-27.74, -27.74) * mm});
            skCircle(sketch, "E53.cCircle", {"center": v(13.87, -13.87) * mm, "radius": 19.61 * mm, "construction": true});
            skLineSegment(sketch, "E53.0", {"start": v(0, -27.74) * mm, "end": v(0, 0) * mm});
            skLineSegment(sketch, "E53.1", {"start": v(0, 0) * mm, "end": v(27.74, 0) * mm});
            skLineSegment(sketch, "E53.2", {"start": v(27.74, 0) * mm, "end": v(27.74, -27.74) * mm});
            skLineSegment(sketch, "E53.3", {"start": v(27.74, -27.74) * mm, "end": v(0, -27.74) * mm});
            skCircle(sketch, "E54.cCircle", {"center": v(41.6, -13.87) * mm, "radius": 19.61 * mm, "construction": true});
            skLineSegment(sketch, "E54.0", {"start": v(27.74, -27.74) * mm, "end": v(27.74, 0) * mm});
            skLineSegment(sketch, "E54.1", {"start": v(27.74, 0) * mm, "end": v(55.48, 0) * mm});
            skLineSegment(sketch, "E54.2", {"start": v(55.48, 0) * mm, "end": v(55.48, -27.74) * mm});
            skLineSegment(sketch, "E54.3", {"start": v(55.48, -27.74) * mm, "end": v(27.74, -27.74) * mm});
            skCircle(sketch, "E55.cCircle", {"center": v(69.34, -13.87) * mm, "radius": 19.61 * mm, "construction": true});
            skLineSegment(sketch, "E55.0", {"start": v(55.48, -27.74) * mm, "end": v(55.48, 0) * mm});
            skLineSegment(sketch, "E55.1", {"start": v(55.48, 0) * mm, "end": v(83.21, 0) * mm});
            skLineSegment(sketch, "E55.2", {"start": v(83.21, 0) * mm, "end": v(83.21, -27.74) * mm});
            skLineSegment(sketch, "E55.3", {"start": v(83.21, -27.74) * mm, "end": v(55.48, -27.74) * mm});
            skCircle(sketch, "E56.cCircle", {"center": v(-69.34, -41.6) * mm, "radius": 19.61 * mm, "construction": true});
            skLineSegment(sketch, "E56.0", {"start": v(-55.48, -27.74) * mm, "end": v(-55.48, -55.48) * mm});
            skLineSegment(sketch, "E56.1", {"start": v(-55.48, -55.48) * mm, "end": v(-83.21, -55.48) * mm});
            skLineSegment(sketch, "E56.2", {"start": v(-83.21, -55.48) * mm, "end": v(-83.21, -27.74) * mm});
            skLineSegment(sketch, "E56.3", {"start": v(-83.21, -27.74) * mm, "end": v(-55.48, -27.74) * mm});
            skCircle(sketch, "E57.cCircle", {"center": v(-41.6, -41.6) * mm, "radius": 19.61 * mm, "construction": true});
            skLineSegment(sketch, "E57.0", {"start": v(-55.48, -27.74) * mm, "end": v(-27.74, -27.74) * mm});
            skLineSegment(sketch, "E57.1", {"start": v(-27.74, -27.74) * mm, "end": v(-27.74, -55.48) * mm});
            skLineSegment(sketch, "E57.2", {"start": v(-27.74, -55.48) * mm, "end": v(-55.48, -55.48) * mm});
            skLineSegment(sketch, "E57.3", {"start": v(-55.48, -55.48) * mm, "end": v(-55.48, -27.74) * mm});
            skCircle(sketch, "E58.cCircle", {"center": v(-13.87, -41.6) * mm, "radius": 19.61 * mm, "construction": true});
            skLineSegment(sketch, "E58.0", {"start": v(0, -27.74) * mm, "end": v(0, -55.48) * mm});
            skLineSegment(sketch, "E58.1", {"start": v(0, -55.48) * mm, "end": v(-27.74, -55.48) * mm});
            skLineSegment(sketch, "E58.2", {"start": v(-27.74, -55.48) * mm, "end": v(-27.74, -27.74) * mm});
            skLineSegment(sketch, "E58.3", {"start": v(-27.74, -27.74) * mm, "end": v(0, -27.74) * mm});
            skCircle(sketch, "E59.cCircle", {"center": v(13.87, -41.6) * mm, "radius": 19.61 * mm, "construction": true});
            skLineSegment(sketch, "E59.0", {"start": v(27.74, -27.74) * mm, "end": v(27.74, -55.48) * mm});
            skLineSegment(sketch, "E59.1", {"start": v(27.74, -55.48) * mm, "end": v(0, -55.48) * mm});
            skLineSegment(sketch, "E59.2", {"start": v(0, -55.48) * mm, "end": v(0, -27.74) * mm});
            skLineSegment(sketch, "E59.3", {"start": v(0, -27.74) * mm, "end": v(27.74, -27.74) * mm});
            skCircle(sketch, "E60.cCircle", {"center": v(41.6, -41.6) * mm, "radius": 19.61 * mm, "construction": true});
            skLineSegment(sketch, "E60.0", {"start": v(55.48, -27.74) * mm, "end": v(55.48, -55.48) * mm});
            skLineSegment(sketch, "E60.1", {"start": v(55.48, -55.48) * mm, "end": v(27.74, -55.48) * mm});
            skLineSegment(sketch, "E60.2", {"start": v(27.74, -55.48) * mm, "end": v(27.74, -27.74) * mm});
            skLineSegment(sketch, "E60.3", {"start": v(27.74, -27.74) * mm, "end": v(55.48, -27.74) * mm});
            skCircle(sketch, "E61.cCircle", {"center": v(69.34, -41.6) * mm, "radius": 19.61 * mm, "construction": true});
            skLineSegment(sketch, "E61.0", {"start": v(55.48, -27.74) * mm, "end": v(83.21, -27.74) * mm});
            skLineSegment(sketch, "E61.1", {"start": v(83.21, -27.74) * mm, "end": v(83.21, -55.48) * mm});
            skLineSegment(sketch, "E61.2", {"start": v(83.21, -55.48) * mm, "end": v(55.48, -55.48) * mm});
            skLineSegment(sketch, "E61.3", {"start": v(55.48, -55.48) * mm, "end": v(55.48, -27.74) * mm});
            skCircle(sketch, "E62.cCircle", {"center": v(-41.6, -69.34) * mm, "radius": 19.61 * mm, "construction": true});
            skLineSegment(sketch, "E62.0", {"start": v(-27.74, -55.48) * mm, "end": v(-27.74, -83.21) * mm});
            skLineSegment(sketch, "E62.1", {"start": v(-27.74, -83.21) * mm, "end": v(-55.48, -83.21) * mm});
            skLineSegment(sketch, "E62.2", {"start": v(-55.48, -83.21) * mm, "end": v(-55.48, -55.48) * mm});
            skLineSegment(sketch, "E62.3", {"start": v(-55.48, -55.48) * mm, "end": v(-27.74, -55.48) * mm});
            skCircle(sketch, "E63.cCircle", {"center": v(-13.87, -69.34) * mm, "radius": 19.61 * mm, "construction": true});
            skLineSegment(sketch, "E63.0", {"start": v(-27.74, -55.48) * mm, "end": v(0, -55.48) * mm});
            skLineSegment(sketch, "E63.1", {"start": v(0, -55.48) * mm, "end": v(0, -83.21) * mm});
            skLineSegment(sketch, "E63.2", {"start": v(0, -83.21) * mm, "end": v(-27.74, -83.21) * mm});
            skLineSegment(sketch, "E63.3", {"start": v(-27.74, -83.21) * mm, "end": v(-27.74, -55.48) * mm});
            skCircle(sketch, "E64.cCircle", {"center": v(13.87, -69.34) * mm, "radius": 19.61 * mm, "construction": true});
            skLineSegment(sketch, "E64.0", {"start": v(27.74, -55.48) * mm, "end": v(27.74, -83.21) * mm});
            skLineSegment(sketch, "E64.1", {"start": v(27.74, -83.21) * mm, "end": v(0, -83.21) * mm});
            skLineSegment(sketch, "E64.2", {"start": v(0, -83.21) * mm, "end": v(0, -55.48) * mm});
            skLineSegment(sketch, "E64.3", {"start": v(0, -55.48) * mm, "end": v(27.74, -55.48) * mm});
            skCircle(sketch, "E65.cCircle", {"center": v(41.6, -69.34) * mm, "radius": 19.61 * mm, "construction": true});
            skLineSegment(sketch, "E65.0", {"start": v(27.74, -55.48) * mm, "end": v(55.48, -55.48) * mm});
            skLineSegment(sketch, "E65.1", {"start": v(55.48, -55.48) * mm, "end": v(55.48, -83.21) * mm});
            skLineSegment(sketch, "E65.2", {"start": v(55.48, -83.21) * mm, "end": v(27.74, -83.21) * mm});
            skLineSegment(sketch, "E65.3", {"start": v(27.74, -83.21) * mm, "end": v(27.74, -55.48) * mm});
            skSolve(sketch);
        }
        {
            var Q0;
            Q0 = qSketchRegion(id + "F2", true);
            extrude(context, id + "F3", {"entities" : qUnion([Q0]), "depth" : 25 * mm});
        }
        {
            var Q0;
            Q0 = qSketchRegion(id + "F0", true);
            extrude(context, id + "F4", {"entities" : qUnion([Q0]), "depth" : 25 * mm});
        }
        {
            var Q0;
            Q0=makeQuery(id+"F4.opExtrude","SWEPT_BODY",BODY,{"disambiguationData":[OSD([sQuery(id+"F0.wireOp",EDGE,"E0.0"),sQuery(id+"F0.wireOp",EDGE,"E0.1"),sQuery(id+"F0.wireOp",EDGE,"E0.2"),sQuery(id+"F0.wireOp",EDGE,"E1.0"),sQuery(id+"F0.wireOp",EDGE,"E1.1"),sQuery(id+"F0.wireOp",EDGE,"E1.2"),sQuery(id+"F0.wireOp",EDGE,"E2.0"),sQuery(id+"F0.wireOp",EDGE,"E2.1"),sQuery(id+"F0.wireOp",EDGE,"E2.2"),sQuery(id+"F0.wireOp",EDGE,"E3.0"),sQuery(id+"F0.wireOp",EDGE,"E3.1"),sQuery(id+"F0.wireOp",EDGE,"E3.2"),sQuery(id+"F0.wireOp",EDGE,"E4.trimOffspring"),sQuery(id+"F0.wireOp",EDGE,"E5.trimOffspring"),sQuery(id+"F0.wireOp",EDGE,"E6.trimOffspring"),sQuery(id+"F0.wireOp",EDGE,"E7.0"),sQuery(id+"F0.wireOp",EDGE,"E7.1"),sQuery(id+"F0.wireOp",EDGE,"E7.2"),sQuery(id+"F0.wireOp",EDGE,"E8.0"),sQuery(id+"F0.wireOp",EDGE,"E8.2"),sQuery(id+"F0.wireOp",EDGE,"E9.0"),sQuery(id+"F0.wireOp",EDGE,"E9.2"),sQuery(id+"F0.wireOp",EDGE,"E10.0"),sQuery(id+"F0.wireOp",EDGE,"E10.2"),sQuery(id+"F0.wireOp",EDGE,"E11.0"),sQuery(id+"F0.wireOp",EDGE,"E11.1"),sQuery(id+"F0.wireOp",EDGE,"E11.2"),sQuery(id+"F0.wireOp",EDGE,"E12.0"),sQuery(id+"F0.wireOp",EDGE,"E12.2"),sQuery(id+"F0.wireOp",EDGE,"E13.0"),sQuery(id+"F0.wireOp",EDGE,"E13.2"),sQuery(id+"F0.wireOp",EDGE,"E14.0"),sQuery(id+"F0.wireOp",EDGE,"E14.1"),sQuery(id+"F0.wireOp",EDGE,"E14.2"),sQuery(id+"F0.wireOp",EDGE,"E15.0"),sQuery(id+"F0.wireOp",EDGE,"E15.2")])]});
            deleteBodies(context, id + "F5", {"entities" : qUnion([Q0])});
        }
        {
            var Q0;
            Q0=makeQuery(id+"F2.imprint","IMPRINT",FACE,{"disambiguationData":[TD([[makeQuery(id+"F2.imprint","IMPRINT",EDGE,{"derivedFrom":sQuery(id+"F2.wireOp",EDGE,"E32.1")}),1.0]])]});
            var Q1;
            Q1=makeQuery(id+"F2.imprint","IMPRINT",FACE,{"disambiguationData":[TD([[makeQuery(id+"F2.imprint","IMPRINT",EDGE,{"derivedFrom":sQuery(id+"F2.wireOp",EDGE,"E32.1")}),-1.0]])]});
            var Q2;
            Q2=makeQuery(id+"F2.imprint","IMPRINT",FACE,{"disambiguationData":[TD([[makeQuery(id+"F2.imprint","IMPRINT",EDGE,{"derivedFrom":sQuery(id+"F2.wireOp",EDGE,"E32.2")}),-1.0]])]});
            var Q3;
            Q3=makeQuery(id+"F2.imprint","IMPRINT",FACE,{"disambiguationData":[TD([[makeQuery(id+"F2.imprint","IMPRINT",EDGE,{"derivedFrom":sQuery(id+"F2.wireOp",EDGE,"E32.2")}),1.0]])]});
            var Q4;
            Q4=makeQuery(id+"F2.imprint","IMPRINT",FACE,{"disambiguationData":[TD([[makeQuery(id+"F2.imprint","IMPRINT",EDGE,{"derivedFrom":sQuery(id+"F2.wireOp",EDGE,"E21.1")}),1.0]])]});
            var Q5;
            Q5=makeQuery(id+"F2.imprint","IMPRINT",FACE,{"disambiguationData":[TD([[makeQuery(id+"F2.imprint","IMPRINT",EDGE,{"derivedFrom":sQuery(id+"F2.wireOp",EDGE,"E21.1")}),-1.0]])]});
            var Q6;
            Q6=makeQuery(id+"F2.imprint","IMPRINT",FACE,{"disambiguationData":[TD([[makeQuery(id+"F2.imprint","IMPRINT",EDGE,{"derivedFrom":sQuery(id+"F2.wireOp",EDGE,"E21.2")}),-1.0]])]});
            var Q7;
            Q7=makeQuery(id+"F2.imprint","IMPRINT",FACE,{"disambiguationData":[TD([[makeQuery(id+"F2.imprint","IMPRINT",EDGE,{"derivedFrom":sQuery(id+"F2.wireOp",EDGE,"E21.2")}),1.0]])]});
            var Q8;
            Q8=makeQuery(id+"F2.imprint","IMPRINT",FACE,{"disambiguationData":[TD([[makeQuery(id+"F2.imprint","IMPRINT",EDGE,{"derivedFrom":sQuery(id+"F2.wireOp",EDGE,"E22.1")}),1.0]])]});
            var Q9;
            Q9=makeQuery(id+"F2.imprint","IMPRINT",FACE,{"disambiguationData":[TD([[makeQuery(id+"F2.imprint","IMPRINT",EDGE,{"derivedFrom":sQuery(id+"F2.wireOp",EDGE,"E22.1")}),-1.0]])]});
            var Q10;
            Q10=makeQuery(id+"F2.imprint","IMPRINT",FACE,{"disambiguationData":[TD([[makeQuery(id+"F2.imprint","IMPRINT",EDGE,{"derivedFrom":sQuery(id+"F2.wireOp",EDGE,"E22.0")}),-1.0]])]});
            var Q11;
            Q11=makeQuery(id+"F2.imprint","IMPRINT",FACE,{"disambiguationData":[TD([[makeQuery(id+"F2.imprint","IMPRINT",EDGE,{"derivedFrom":sQuery(id+"F2.wireOp",EDGE,"E22.0")}),1.0]])]});
            var Q12;
            Q12=makeQuery(id+"F2.imprint","IMPRINT",FACE,{"disambiguationData":[TD([[makeQuery(id+"F2.imprint","IMPRINT",EDGE,{"derivedFrom":sQuery(id+"F2.wireOp",EDGE,"E24.3")}),1.0]])]});
            var Q13;
            Q13=makeQuery(id+"F2.imprint","IMPRINT",FACE,{"disambiguationData":[TD([[makeQuery(id+"F2.imprint","IMPRINT",EDGE,{"derivedFrom":sQuery(id+"F2.wireOp",EDGE,"E24.3")}),-1.0]])]});
            var Q14;
            Q14=makeQuery(id+"F2.imprint","IMPRINT",FACE,{"disambiguationData":[TD([[makeQuery(id+"F2.imprint","IMPRINT",EDGE,{"derivedFrom":sQuery(id+"F2.wireOp",EDGE,"E32.3")}),1.0]])]});
            var Q15;
            Q15=makeQuery(id+"F2.imprint","IMPRINT",FACE,{"disambiguationData":[TD([[makeQuery(id+"F2.imprint","IMPRINT",EDGE,{"derivedFrom":sQuery(id+"F2.wireOp",EDGE,"E32.3")}),-1.0]])]});
            var Q16;
            Q16=makeQuery(id+"F2.imprint","IMPRINT",FACE,{"disambiguationData":[TD([[makeQuery(id+"F2.imprint","IMPRINT",EDGE,{"derivedFrom":sQuery(id+"F2.wireOp",EDGE,"E32.0")}),-1.0]])]});
            var Q17;
            Q17=makeQuery(id+"F2.imprint","IMPRINT",FACE,{"disambiguationData":[TD([[makeQuery(id+"F2.imprint","IMPRINT",EDGE,{"derivedFrom":sQuery(id+"F2.wireOp",EDGE,"E32.0")}),1.0]])]});
            var Q18;
            Q18=makeQuery(id+"F2.imprint","IMPRINT",FACE,{"disambiguationData":[TD([[makeQuery(id+"F2.imprint","IMPRINT",EDGE,{"derivedFrom":sQuery(id+"F2.wireOp",EDGE,"E31.2")}),-1.0]])]});
            var Q19;
            Q19=makeQuery(id+"F2.imprint","IMPRINT",FACE,{"disambiguationData":[TD([[makeQuery(id+"F2.imprint","IMPRINT",EDGE,{"derivedFrom":sQuery(id+"F2.wireOp",EDGE,"E31.2")}),1.0]])]});
            var Q20;
            Q20=makeQuery(id+"F2.imprint","IMPRINT",FACE,{"disambiguationData":[TD([[makeQuery(id+"F2.imprint","IMPRINT",EDGE,{"derivedFrom":sQuery(id+"F2.wireOp",EDGE,"E31.1")}),1.0]])]});
            var Q21;
            Q21=makeQuery(id+"F2.imprint","IMPRINT",FACE,{"disambiguationData":[TD([[makeQuery(id+"F2.imprint","IMPRINT",EDGE,{"derivedFrom":sQuery(id+"F2.wireOp",EDGE,"E31.1")}),-1.0]])]});
            var Q22;
            Q22=makeQuery(id+"F2.imprint","IMPRINT",FACE,{"disambiguationData":[TD([[makeQuery(id+"F2.imprint","IMPRINT",EDGE,{"derivedFrom":sQuery(id+"F2.wireOp",EDGE,"E31.0")}),-1.0]])]});
            var Q23;
            Q23=makeQuery(id+"F2.imprint","IMPRINT",FACE,{"disambiguationData":[TD([[makeQuery(id+"F2.imprint","IMPRINT",EDGE,{"derivedFrom":sQuery(id+"F2.wireOp",EDGE,"E31.0")}),1.0]])]});
            var Q24;
            Q24=makeQuery(id+"F2.imprint","IMPRINT",FACE,{"disambiguationData":[TD([[makeQuery(id+"F2.imprint","IMPRINT",EDGE,{"derivedFrom":sQuery(id+"F2.wireOp",EDGE,"E30.2")}),-1.0]])]});
            var Q25;
            Q25=makeQuery(id+"F2.imprint","IMPRINT",FACE,{"disambiguationData":[TD([[makeQuery(id+"F2.imprint","IMPRINT",EDGE,{"derivedFrom":sQuery(id+"F2.wireOp",EDGE,"E30.2")}),1.0]])]});
            var Q26;
            Q26=makeQuery(id+"F2.imprint","IMPRINT",FACE,{"disambiguationData":[TD([[makeQuery(id+"F2.imprint","IMPRINT",EDGE,{"derivedFrom":sQuery(id+"F2.wireOp",EDGE,"E23.3")}),1.0]])]});
            var Q27;
            Q27=makeQuery(id+"F2.imprint","IMPRINT",FACE,{"disambiguationData":[TD([[makeQuery(id+"F2.imprint","IMPRINT",EDGE,{"derivedFrom":sQuery(id+"F2.wireOp",EDGE,"E23.3")}),-1.0]])]});
            var Q28;
            Q28=makeQuery(id+"F2.imprint","IMPRINT",FACE,{"disambiguationData":[TD([[makeQuery(id+"F2.imprint","IMPRINT",EDGE,{"derivedFrom":sQuery(id+"F2.wireOp",EDGE,"E23.0")}),-1.0]])]});
            var Q29;
            Q29=makeQuery(id+"F2.imprint","IMPRINT",FACE,{"disambiguationData":[TD([[makeQuery(id+"F2.imprint","IMPRINT",EDGE,{"derivedFrom":sQuery(id+"F2.wireOp",EDGE,"E23.0")}),1.0]])]});
            var Q30;
            Q30=makeQuery(id+"F2.imprint","IMPRINT",FACE,{"disambiguationData":[TD([[makeQuery(id+"F2.imprint","IMPRINT",EDGE,{"derivedFrom":sQuery(id+"F2.wireOp",EDGE,"E22.2")}),-1.0]])]});
            var Q31;
            Q31=makeQuery(id+"F2.imprint","IMPRINT",FACE,{"disambiguationData":[TD([[makeQuery(id+"F2.imprint","IMPRINT",EDGE,{"derivedFrom":sQuery(id+"F2.wireOp",EDGE,"E22.2")}),1.0]])]});
            var Q32;
            Q32=makeQuery(id+"F2.imprint","IMPRINT",FACE,{"disambiguationData":[TD([[makeQuery(id+"F2.imprint","IMPRINT",EDGE,{"derivedFrom":sQuery(id+"F2.wireOp",EDGE,"E25.1")}),1.0]])]});
            var Q33;
            Q33=makeQuery(id+"F2.imprint","IMPRINT",FACE,{"disambiguationData":[TD([[makeQuery(id+"F2.imprint","IMPRINT",EDGE,{"derivedFrom":sQuery(id+"F2.wireOp",EDGE,"E25.1")}),-1.0]])]});
            var Q34;
            Q34=makeQuery(id+"F2.imprint","IMPRINT",FACE,{"disambiguationData":[TD([[makeQuery(id+"F2.imprint","IMPRINT",EDGE,{"derivedFrom":sQuery(id+"F2.wireOp",EDGE,"E25.0")}),-1.0]])]});
            var Q35;
            Q35=makeQuery(id+"F2.imprint","IMPRINT",FACE,{"disambiguationData":[TD([[makeQuery(id+"F2.imprint","IMPRINT",EDGE,{"derivedFrom":sQuery(id+"F2.wireOp",EDGE,"E25.0")}),1.0]])]});
            var Q36;
            Q36=makeQuery(id+"F2.imprint","IMPRINT",FACE,{"disambiguationData":[TD([[makeQuery(id+"F2.imprint","IMPRINT",EDGE,{"derivedFrom":sQuery(id+"F2.wireOp",EDGE,"E27.3")}),1.0]])]});
            var Q37;
            Q37=makeQuery(id+"F2.imprint","IMPRINT",FACE,{"disambiguationData":[TD([[makeQuery(id+"F2.imprint","IMPRINT",EDGE,{"derivedFrom":sQuery(id+"F2.wireOp",EDGE,"E27.3")}),-1.0]])]});
            var Q38;
            Q38=makeQuery(id+"F2.imprint","IMPRINT",FACE,{"disambiguationData":[TD([[makeQuery(id+"F2.imprint","IMPRINT",EDGE,{"derivedFrom":sQuery(id+"F2.wireOp",EDGE,"E30.3")}),1.0]])]});
            var Q39;
            Q39=makeQuery(id+"F2.imprint","IMPRINT",FACE,{"disambiguationData":[TD([[makeQuery(id+"F2.imprint","IMPRINT",EDGE,{"derivedFrom":sQuery(id+"F2.wireOp",EDGE,"E30.3")}),-1.0]])]});
            var Q40;
            Q40=makeQuery(id+"F2.imprint","IMPRINT",FACE,{"disambiguationData":[TD([[makeQuery(id+"F2.imprint","IMPRINT",EDGE,{"derivedFrom":sQuery(id+"F2.wireOp",EDGE,"E30.0")}),-1.0]])]});
            var Q41;
            Q41=makeQuery(id+"F2.imprint","IMPRINT",FACE,{"disambiguationData":[TD([[makeQuery(id+"F2.imprint","IMPRINT",EDGE,{"derivedFrom":sQuery(id+"F2.wireOp",EDGE,"E30.0")}),1.0]])]});
            var Q42;
            Q42=makeQuery(id+"F2.imprint","IMPRINT",FACE,{"disambiguationData":[TD([[makeQuery(id+"F2.imprint","IMPRINT",EDGE,{"derivedFrom":sQuery(id+"F2.wireOp",EDGE,"E29.2")}),-1.0]])]});
            var Q43;
            Q43=makeQuery(id+"F2.imprint","IMPRINT",FACE,{"disambiguationData":[TD([[makeQuery(id+"F2.imprint","IMPRINT",EDGE,{"derivedFrom":sQuery(id+"F2.wireOp",EDGE,"E29.2")}),1.0]])]});
            var Q44;
            Q44=makeQuery(id+"F2.imprint","IMPRINT",FACE,{"disambiguationData":[TD([[makeQuery(id+"F2.imprint","IMPRINT",EDGE,{"derivedFrom":sQuery(id+"F2.wireOp",EDGE,"E29.1")}),-1.0]])]});
            var Q45;
            Q45=makeQuery(id+"F2.imprint","IMPRINT",FACE,{"disambiguationData":[TD([[makeQuery(id+"F2.imprint","IMPRINT",EDGE,{"derivedFrom":sQuery(id+"F2.wireOp",EDGE,"E29.1")}),1.0]])]});
            var Q46;
            Q46=makeQuery(id+"F2.imprint","IMPRINT",FACE,{"disambiguationData":[TD([[makeQuery(id+"F2.imprint","IMPRINT",EDGE,{"derivedFrom":sQuery(id+"F2.wireOp",EDGE,"E29.0")}),-1.0]])]});
            var Q47;
            Q47=makeQuery(id+"F2.imprint","IMPRINT",FACE,{"disambiguationData":[TD([[makeQuery(id+"F2.imprint","IMPRINT",EDGE,{"derivedFrom":sQuery(id+"F2.wireOp",EDGE,"E29.0")}),1.0]])]});
            var Q48;
            Q48=makeQuery(id+"F2.imprint","IMPRINT",FACE,{"disambiguationData":[TD([[makeQuery(id+"F2.imprint","IMPRINT",EDGE,{"derivedFrom":sQuery(id+"F2.wireOp",EDGE,"E28.0")}),-1.0]])]});
            var Q49;
            Q49=makeQuery(id+"F2.imprint","IMPRINT",FACE,{"disambiguationData":[TD([[makeQuery(id+"F2.imprint","IMPRINT",EDGE,{"derivedFrom":sQuery(id+"F2.wireOp",EDGE,"E28.0")}),1.0]])]});
            var Q50;
            Q50=makeQuery(id+"F2.imprint","IMPRINT",FACE,{"disambiguationData":[TD([[makeQuery(id+"F2.imprint","IMPRINT",EDGE,{"derivedFrom":sQuery(id+"F2.wireOp",EDGE,"E27.0")}),-1.0]])]});
            var Q51;
            Q51=makeQuery(id+"F2.imprint","IMPRINT",FACE,{"disambiguationData":[TD([[makeQuery(id+"F2.imprint","IMPRINT",EDGE,{"derivedFrom":sQuery(id+"F2.wireOp",EDGE,"E27.0")}),1.0]])]});
            var Q52;
            Q52=makeQuery(id+"F2.imprint","IMPRINT",FACE,{"disambiguationData":[TD([[makeQuery(id+"F2.imprint","IMPRINT",EDGE,{"derivedFrom":sQuery(id+"F2.wireOp",EDGE,"E26.0")}),-1.0]])]});
            var Q53;
            Q53=makeQuery(id+"F2.imprint","IMPRINT",FACE,{"disambiguationData":[TD([[makeQuery(id+"F2.imprint","IMPRINT",EDGE,{"derivedFrom":sQuery(id+"F2.wireOp",EDGE,"E26.0")}),1.0]])]});
            var Q54;
            Q54=makeQuery(id+"F2.imprint","IMPRINT",FACE,{"disambiguationData":[TD([[makeQuery(id+"F2.imprint","IMPRINT",EDGE,{"derivedFrom":sQuery(id+"F2.wireOp",EDGE,"E25.2")}),-1.0]])]});
            var Q55;
            Q55=makeQuery(id+"F2.imprint","IMPRINT",FACE,{"disambiguationData":[TD([[makeQuery(id+"F2.imprint","IMPRINT",EDGE,{"derivedFrom":sQuery(id+"F2.wireOp",EDGE,"E25.2")}),1.0]])]});
            var Q56;
            Q56=makeQuery(id+"F2.imprint","IMPRINT",FACE,{"disambiguationData":[TD([[makeQuery(id+"F2.imprint","IMPRINT",EDGE,{"derivedFrom":sQuery(id+"F2.wireOp",EDGE,"E26.1")}),1.0]])]});
            var Q57;
            Q57=makeQuery(id+"F2.imprint","IMPRINT",FACE,{"disambiguationData":[TD([[makeQuery(id+"F2.imprint","IMPRINT",EDGE,{"derivedFrom":sQuery(id+"F2.wireOp",EDGE,"E26.1")}),-1.0]])]});
            var Q58;
            Q58=makeQuery(id+"F2.imprint","IMPRINT",FACE,{"disambiguationData":[TD([[makeQuery(id+"F2.imprint","IMPRINT",EDGE,{"derivedFrom":sQuery(id+"F2.wireOp",EDGE,"E26.2")}),-1.0]])]});
            var Q59;
            Q59=makeQuery(id+"F2.imprint","IMPRINT",FACE,{"disambiguationData":[TD([[makeQuery(id+"F2.imprint","IMPRINT",EDGE,{"derivedFrom":sQuery(id+"F2.wireOp",EDGE,"E26.2")}),1.0]])]});
            var Q60;
            Q60=makeQuery(id+"F2.imprint","IMPRINT",FACE,{"disambiguationData":[TD([[makeQuery(id+"F2.imprint","IMPRINT",EDGE,{"derivedFrom":sQuery(id+"F2.wireOp",EDGE,"E28.1")}),1.0]])]});
            var Q61;
            Q61=makeQuery(id+"F2.imprint","IMPRINT",FACE,{"disambiguationData":[TD([[makeQuery(id+"F2.imprint","IMPRINT",EDGE,{"derivedFrom":sQuery(id+"F2.wireOp",EDGE,"E28.1")}),-1.0]])]});
            var Q62;
            Q62=makeQuery(id+"F2.imprint","IMPRINT",FACE,{"disambiguationData":[TD([[makeQuery(id+"F2.imprint","IMPRINT",EDGE,{"derivedFrom":sQuery(id+"F2.wireOp",EDGE,"E28.2")}),-1.0]])]});
            var Q63;
            Q63=makeQuery(id+"F2.imprint","IMPRINT",FACE,{"disambiguationData":[TD([[makeQuery(id+"F2.imprint","IMPRINT",EDGE,{"derivedFrom":sQuery(id+"F2.wireOp",EDGE,"E28.2")}),1.0]])]});
            extrude(context, id + "F6", {"entities" : qUnion([Q0, Q1, Q2, Q3, Q4, Q5, Q6, Q7, Q8, Q9, Q10, Q11, Q12, Q13, Q14, Q15, Q16, Q17, Q18, Q19, Q20, Q21, Q22, Q23, Q24, Q25, Q26, Q27, Q28, Q29, Q30, Q31, Q32, Q33, Q34, Q35, Q36, Q37, Q38, Q39, Q40, Q41, Q42, Q43, Q44, Q45, Q46, Q47, Q48, Q49, Q50, Q51, Q52, Q53, Q54, Q55, Q56, Q57, Q58, Q59, Q60, Q61, Q62, Q63]), "depth" : 25 * mm});
        }
    });
